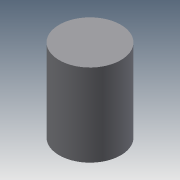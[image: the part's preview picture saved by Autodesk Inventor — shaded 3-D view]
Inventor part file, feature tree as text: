
AUTODESK INVENTOR PART (.ipt)
format: ipt  version: 2013 (Build 170138000, 138)  size: 79,872 bytes
history: native  units: mm
features: sketch x3, extrude x1, plane x1, hole x1
ambient origin geometry x8: Origin, YZ Plane, XZ Plane, XY Plane, X Axis, Y Axis, Z Axis, Center Point
bodies: Solid1 (feature_tree)
feature tree (6):
  extrude  "Extrusion1"  Depth=15.0mm TaperAngle=0.0deg
  plane  "Work Plane1"
  hole  "Hole1"  [1 undecoded]
  sketch  "Sketch4"  dims[d10=2.459mm d11=5.6mm d12=4.0mm d13=2.0mm d14=90.0deg d15=5.6mm d16=0.0mm]
  sketch  "Sketch1"  dims[d0=11.2mm d1=15.0mm d2=0.0mm]
  sketch  "Sketch3"  dims[d9=2.4mm]
note: 1 required parameter value undecoded (feature->parameter linkage not recoverable at this tier; creation-order binding heuristic only, values carry confidence <= 0.55)
